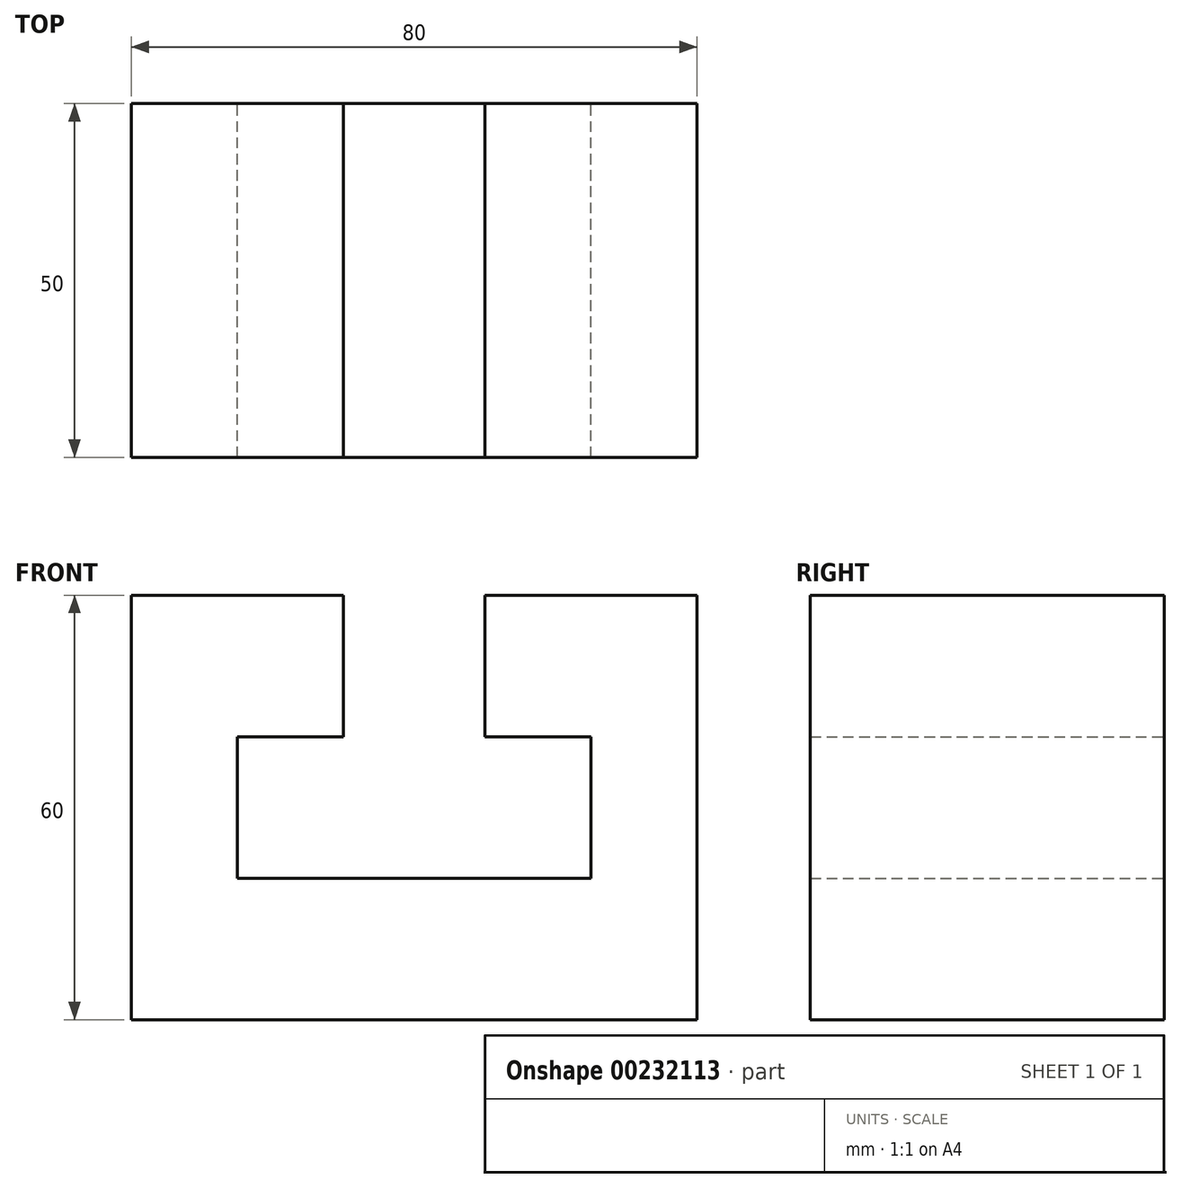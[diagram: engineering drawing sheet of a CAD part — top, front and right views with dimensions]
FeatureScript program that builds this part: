
annotation { "Feature Type Name" : "Feature", "Feature Type Description" : "" }
export const myFeature = defineFeature(function(context is Context, id is Id, definition is map)
    precondition{}
    {
        {
            var Q0;
            Q0=qCreatedBy(makeId("Front.planeOp"),FACE);
            var sketch = newSketch(context, id + "F0", { "sketchPlane" : qUnion([Q0])});
            skLineSegment(sketch, "E0", {"start": v(-40, 0) * mm, "end": v(-40, 21.92) * mm, "construction": true});
            skLineSegment(sketch, "E1", {"start": v(-40, 0) * mm, "end": v(-80, 0) * mm});
            skLineSegment(sketch, "E2", {"start": v(-80, 0) * mm, "end": v(-80, 60) * mm});
            skLineSegment(sketch, "E3", {"start": v(-80, 60) * mm, "end": v(-50, 60) * mm});
            skLineSegment(sketch, "E4", {"start": v(-50, 60) * mm, "end": v(-50, 40) * mm});
            skLineSegment(sketch, "E5", {"start": v(-50, 40) * mm, "end": v(-65, 40) * mm});
            skLineSegment(sketch, "E6", {"start": v(-65, 40) * mm, "end": v(-65, 20) * mm});
            skLineSegment(sketch, "E7", {"start": v(-65, 20) * mm, "end": v(-40, 20) * mm});
            skLineSegment(sketch, "E8.MirrorCS", {"start": v(-40, 0) * mm, "end": v(0, 0) * mm});
            skLineSegment(sketch, "E9.MirrorCS", {"start": v(-15, 20) * mm, "end": v(-40, 20) * mm});
            skLineSegment(sketch, "E10.MirrorCS", {"start": v(-15, 40) * mm, "end": v(-15, 20) * mm});
            skLineSegment(sketch, "E11.MirrorCS", {"start": v(0, 0) * mm, "end": v(0, 60) * mm});
            skLineSegment(sketch, "E12.MirrorCS", {"start": v(-30, 60) * mm, "end": v(-30, 40) * mm});
            skLineSegment(sketch, "E13.MirrorCS", {"start": v(0, 60) * mm, "end": v(-30, 60) * mm});
            skLineSegment(sketch, "E14.MirrorCS", {"start": v(-30, 40) * mm, "end": v(-15, 40) * mm});
            skSolve(sketch);
        }
        {
            var Q0;
            Q0=makeQuery(id+"F0.imprint","IMPRINT",FACE,{"disambiguationData":[TD([[makeQuery(id+"F0.imprint","IMPRINT",EDGE,{"derivedFrom":sQuery(id+"F0.wireOp",EDGE,"E1")}),-1.0]])]});
            extrude(context, id + "F1", {"entities" : qUnion([Q0]), "depth" : 50 * mm});
        }
    });
